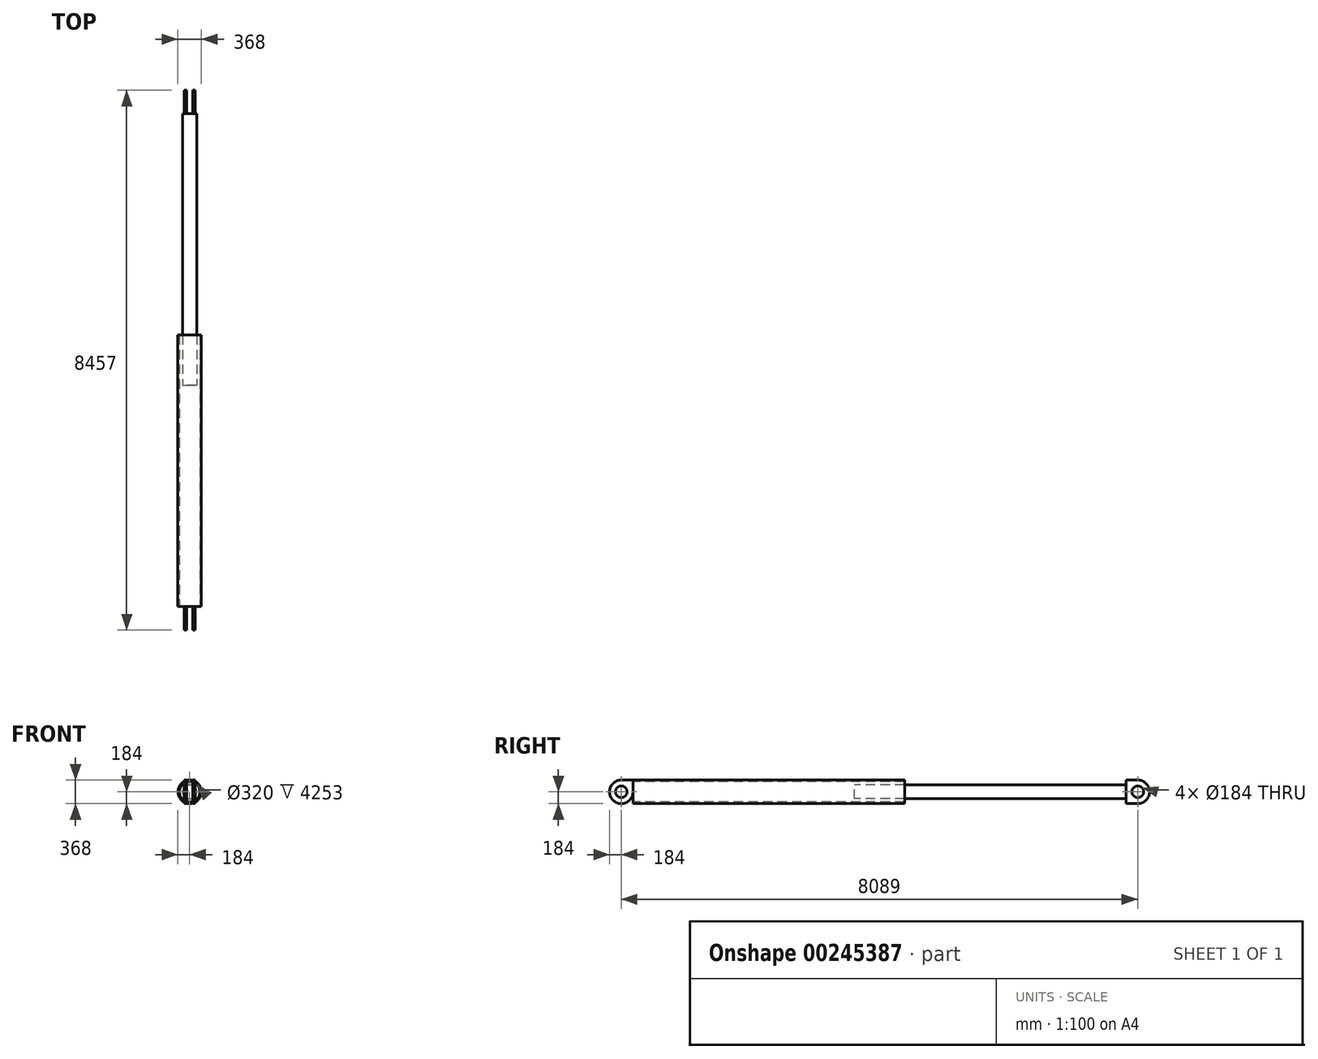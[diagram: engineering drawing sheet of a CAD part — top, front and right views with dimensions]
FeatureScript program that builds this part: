
annotation { "Feature Type Name" : "Feature", "Feature Type Description" : "" }
export const myFeature = defineFeature(function(context is Context, id is Id, definition is map)
    precondition{}
    {
        {
            var Q0;
            Q0=qCreatedBy(makeId("Right.planeOp"),FACE);
            var sketch = newSketch(context, id + "F0", { "sketchPlane" : qUnion([Q0])});
            skCircle(sketch, "E0", {"center": v(0, 0) * mm, "radius": 92 * mm});
            skCircle(sketch, "E1", {"center": v(0, 0) * mm, "radius": 184 * mm});
            skCircle(sketch, "E2", {"center": v(8089, 0) * mm, "radius": 92 * mm});
            skCircle(sketch, "E3", {"center": v(8089, 0) * mm, "radius": 184 * mm});
            skLineSegment(sketch, "E4", {"start": v(0, 0) * mm, "end": v(0, 92) * mm, "construction": true});
            skLineSegment(sketch, "E5", {"start": v(0, 92) * mm, "end": v(0, 184) * mm, "construction": true});
            skLineSegment(sketch, "E6", {"start": v(0, 0) * mm, "end": v(8089, 0) * mm, "construction": true});
            skLineSegment(sketch, "E7", {"start": v(184, 184) * mm, "end": v(184, -184) * mm});
            skLineSegment(sketch, "E8", {"start": v(0, -184) * mm, "end": v(184, -184) * mm});
            skLineSegment(sketch, "E9", {"start": v(184, 184) * mm, "end": v(0, 184) * mm});
            skLineSegment(sketch, "E10", {"start": v(8089, 184) * mm, "end": v(7905, 184) * mm});
            skLineSegment(sketch, "E11", {"start": v(7905, 184) * mm, "end": v(7905, -184) * mm});
            skLineSegment(sketch, "E12", {"start": v(8089, -184) * mm, "end": v(7905, -184) * mm});
            skLineSegment(sketch, "E13", {"start": v(8089, 0) * mm, "end": v(8089, 92) * mm, "construction": true});
            skLineSegment(sketch, "E14", {"start": v(8089, 92) * mm, "end": v(8089, 184) * mm, "construction": true});
            skLineSegment(sketch, "E15.bottom", {"start": v(184, 0) * mm, "end": v(4437, 0) * mm});
            skLineSegment(sketch, "E15.top", {"start": v(184, 184) * mm, "end": v(4437, 184) * mm});
            skLineSegment(sketch, "E15.left", {"start": v(184, 0) * mm, "end": v(184, 184) * mm});
            skLineSegment(sketch, "E15.right", {"start": v(4437, 0) * mm, "end": v(4437, 184) * mm});
            skLineSegment(sketch, "E16.top", {"start": v(184, 160) * mm, "end": v(4437, 160) * mm});
            skLineSegment(sketch, "E16.left", {"start": v(184, 0) * mm, "end": v(184, 160) * mm});
            skLineSegment(sketch, "E16.right", {"start": v(4437, 0) * mm, "end": v(4437, 160) * mm});
            skLineSegment(sketch, "E17.top", {"start": v(4437, 0) * mm, "end": v(7905, 0) * mm});
            skLineSegment(sketch, "E18", {"start": v(4437, 184) * mm, "end": v(4621, 184) * mm, "construction": true});
            skLineSegment(sketch, "E19", {"start": v(7905, -110) * mm, "end": v(3652, -110) * mm});
            skLineSegment(sketch, "E20", {"start": v(3652, -110) * mm, "end": v(3468, -110) * mm, "construction": true});
            skLineSegment(sketch, "E21", {"start": v(3652, -110) * mm, "end": v(3652, 0) * mm});
            skLineSegment(sketch, "E22", {"start": v(0, -621.93) * mm, "end": v(4621, -621.93) * mm, "construction": true});
            skLineSegment(sketch, "E23", {"start": v(3468, -445.19) * mm, "end": v(8089, -445.19) * mm, "construction": true});
            skSolve(sketch);
        }
        {
            var Q0;
            Q0=makeQuery(id+"F0.imprint","IMPRINT",FACE,{"disambiguationData":[TD([[makeQuery(id+"F0.imprint","IMPRINT",EDGE,{"derivedFrom":sQuery(id+"F0.wireOp",EDGE,"E15.top")}),-1.0]])]});
            var Q1;
            Q1=sQuery(id+"F0.wireOp",EDGE,"E15.bottom");
            revolve(context, id + "F1", {"entities" : qUnion([Q0]), "axis" : qUnion([Q1]), "revolveType" : RevolveType.FULL});
        }
        {
            var Q0;
            {var subQ1=sQuery(id+"F0.wireOp",EDGE,"E17.top");Q0=makeQuery(id+"F0.imprint","IMPRINT",FACE,{"disambiguationData":[TD([[makeQuery(id+"F0.imprint","IMPRINT",EDGE,{"derivedFrom":subQ1}),-1.0]])]});}
            var Q1;
            Q1=sQuery(id+"F0.wireOp",EDGE,"E17.top");
            revolve(context, id + "F2", {"entities" : qUnion([Q0]), "axis" : qUnion([Q1]), "revolveType" : RevolveType.FULL});
        }
        {
            var Q0;
            Q0=makeQuery(id+"F0.imprint","IMPRINT",FACE,{"disambiguationData":[TD([[makeQuery(id+"F0.imprint","IMPRINT",EDGE,{"derivedFrom":sQuery(id+"F0.wireOp",EDGE,"E0")}),-1.0]])]});
            var Q1;
            {var subQ2=sQuery(id+"F0.wireOp",EDGE,"E9");Q1=makeQuery(id+"F0.imprint","IMPRINT",FACE,{"disambiguationData":[TD([[makeQuery(id+"F0.imprint","IMPRINT",EDGE,{"derivedFrom":subQ2}),1.0]])]});}
            var Q2;
            {var subQ0=sQuery(id+"F0.wireOp",EDGE,"E7");Q2=makeQuery(id+"F0.imprint","IMPRINT",FACE,{"disambiguationData":[TD([[makeQuery(id+"F0.imprint","IMPRINT",EDGE,{"derivedFrom":subQ0}),-1.0]])]});}
            extrude(context, id + "F3", {"entities" : qUnion([Q0, Q1, Q2]), "operationType" : NewBodyOperationType.ADD, "endBound" : BoundingType.SYMMETRIC, "offsetDistance" : 25 * mm, "depth" : 170 * mm});
        }
        {
            var Q0;
            Q0=makeQuery(id+"F0.imprint","IMPRINT",FACE,{"disambiguationData":[TD([[makeQuery(id+"F0.imprint","IMPRINT",EDGE,{"derivedFrom":sQuery(id+"F0.wireOp",EDGE,"E0")}),-1.0]])]});
            var Q1;
            {var subQ2=sQuery(id+"F0.wireOp",EDGE,"E9");Q1=makeQuery(id+"F0.imprint","IMPRINT",FACE,{"disambiguationData":[TD([[makeQuery(id+"F0.imprint","IMPRINT",EDGE,{"derivedFrom":subQ2}),1.0]])]});}
            var Q2;
            {var subQ0=sQuery(id+"F0.wireOp",EDGE,"E7");Q2=makeQuery(id+"F0.imprint","IMPRINT",FACE,{"disambiguationData":[TD([[makeQuery(id+"F0.imprint","IMPRINT",EDGE,{"derivedFrom":subQ0}),-1.0]])]});}
            extrude(context, id + "F4", {"entities" : qUnion([Q0, Q1, Q2]), "operationType" : NewBodyOperationType.REMOVE, "endBound" : BoundingType.SYMMETRIC, "oppositeDirection" : true, "depth" : 100 * mm, "offsetDistance" : 25 * mm});
        }
        {
            var Q0;
            Q0=makeQuery(id+"F0.imprint","IMPRINT",FACE,{"disambiguationData":[TD([[makeQuery(id+"F0.imprint","IMPRINT",EDGE,{"derivedFrom":sQuery(id+"F0.wireOp",EDGE,"E2")}),-1.0]])]});
            var Q1;
            {var subQ0=sQuery(id+"F0.wireOp",EDGE,"E10");Q1=makeQuery(id+"F0.imprint","IMPRINT",FACE,{"disambiguationData":[TD([[makeQuery(id+"F0.imprint","IMPRINT",EDGE,{"derivedFrom":subQ0}),1.0]])]});}
            var Q2;
            {var subQ0=sQuery(id+"F0.wireOp",EDGE,"E12");Q2=makeQuery(id+"F0.imprint","IMPRINT",FACE,{"disambiguationData":[TD([[makeQuery(id+"F0.imprint","IMPRINT",EDGE,{"derivedFrom":subQ0}),-1.0]])]});}
            extrude(context, id + "F5", {"entities" : qUnion([Q0, Q1, Q2]), "operationType" : NewBodyOperationType.ADD, "endBound" : BoundingType.SYMMETRIC, "offsetDistance" : 25 * mm, "depth" : 170 * mm});
        }
        {
            var Q0;
            {var subQ0=sQuery(id+"F0.wireOp",EDGE,"E10");Q0=makeQuery(id+"F0.imprint","IMPRINT",FACE,{"disambiguationData":[TD([[makeQuery(id+"F0.imprint","IMPRINT",EDGE,{"derivedFrom":subQ0}),1.0]])]});}
            var Q1;
            Q1=makeQuery(id+"F0.imprint","IMPRINT",FACE,{"disambiguationData":[TD([[makeQuery(id+"F0.imprint","IMPRINT",EDGE,{"derivedFrom":sQuery(id+"F0.wireOp",EDGE,"E2")}),-1.0]])]});
            var Q2;
            {var subQ0=sQuery(id+"F0.wireOp",EDGE,"E12");Q2=makeQuery(id+"F0.imprint","IMPRINT",FACE,{"disambiguationData":[TD([[makeQuery(id+"F0.imprint","IMPRINT",EDGE,{"derivedFrom":subQ0}),-1.0]])]});}
            extrude(context, id + "F6", {"entities" : qUnion([Q0, Q1, Q2]), "operationType" : NewBodyOperationType.REMOVE, "endBound" : BoundingType.SYMMETRIC, "oppositeDirection" : true, "depth" : 100 * mm, "offsetDistance" : 25 * mm});
        }
        {
            var Q0;
            Q0=makeQuery(id+"F0.imprint","IMPRINT",FACE,{"disambiguationData":[TD([[makeQuery(id+"F0.imprint","IMPRINT",EDGE,{"derivedFrom":sQuery(id+"F0.wireOp",EDGE,"E16.top")}),-1.0]])]});
            var Q1;
            Q1=sQuery(id+"F0.wireOp",EDGE,"E15.bottom");
            revolve(context, id + "F7", {"surfaceOperationType" : NewSurfaceOperationType.NEW, "entities" : qUnion([Q0]), "axis" : qUnion([Q1]), "revolveType" : RevolveType.FULL});
        }
    });
